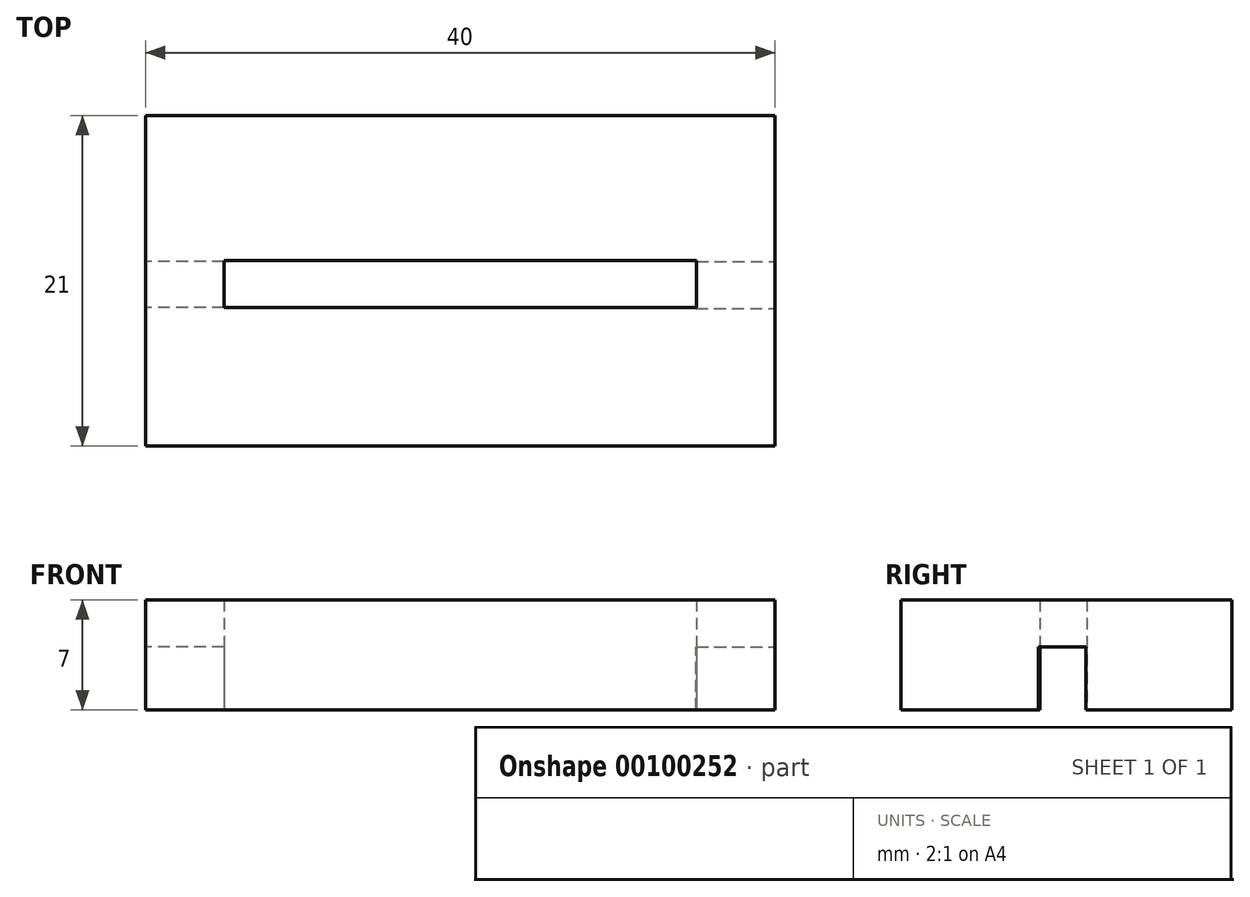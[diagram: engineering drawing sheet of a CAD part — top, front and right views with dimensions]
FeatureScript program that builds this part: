
annotation { "Feature Type Name" : "Feature", "Feature Type Description" : "" }
export const myFeature = defineFeature(function(context is Context, id is Id, definition is map)
    precondition{}
    {
        {
            var Q0;
            Q0=qCreatedBy(makeId("Top.planeOp"),FACE);
            var sketch = newSketch(context, id + "F0", { "sketchPlane" : qUnion([Q0])});
            skLineSegment(sketch, "E0.bottom", {"start": v(0, 0) * mm, "end": v(-40, 0) * mm});
            skLineSegment(sketch, "E0.top", {"start": v(0, -21) * mm, "end": v(-40, -21) * mm});
            skLineSegment(sketch, "E0.left", {"start": v(0, 0) * mm, "end": v(0, -21) * mm});
            skLineSegment(sketch, "E0.right", {"start": v(-40, 0) * mm, "end": v(-40, -21) * mm});
            skLineSegment(sketch, "E1", {"start": v(-20, -9.2) * mm, "end": v(-35, -9.2) * mm});
            skLineSegment(sketch, "E2", {"start": v(-35, -9.2) * mm, "end": v(-5, -9.2) * mm});
            skLineSegment(sketch, "E3", {"start": v(-5, -10.5) * mm, "end": v(-5, -12.2) * mm});
            skLineSegment(sketch, "E4", {"start": v(-5, -12.2) * mm, "end": v(-5, -9.2) * mm});
            skLineSegment(sketch, "E5", {"start": v(-20, -12.2) * mm, "end": v(-35, -12.2) * mm});
            skLineSegment(sketch, "E6", {"start": v(-35, -12.2) * mm, "end": v(-5, -12.2) * mm});
            skLineSegment(sketch, "E7.bottom", {"start": v(-35, -10.5) * mm, "end": v(-35, -10.5) * mm});
            skLineSegment(sketch, "E7.top", {"start": v(-35, -39.85) * mm, "end": v(-35, -39.85) * mm});
            skLineSegment(sketch, "E7.right", {"start": v(-35, -10.5) * mm, "end": v(-35, -12.2) * mm});
            skLineSegment(sketch, "E8.top", {"start": v(-35, 17) * mm, "end": v(-35, 17) * mm});
            skLineSegment(sketch, "E8.left", {"start": v(-35, -12.2) * mm, "end": v(-35, -9.2) * mm});
            skPoint(sketch, "E9.start.orphan", {"position": v(-20, -21) * mm});
            skPoint(sketch, "E10.start.orphan", {"position": v(0, -10.5) * mm});
            skLineSegment(sketch, "E11.right", {"start": v(0, -8.8) * mm, "end": v(0, -12.2) * mm});
            skPoint(sketch, "E12.oppositeSnap0", {"position": v(-40, -10.5) * mm});
            skLineSegment(sketch, "E12.right", {"start": v(-40, -8.8) * mm, "end": v(-40, -12.2) * mm});
            skSolve(sketch);
        }
        {
            var Q0;
            Q0=makeQuery(id+"F0.imprint","IMPRINT",FACE,{"disambiguationData":[TD([[makeQuery(id+"F0.imprint","IMPRINT",EDGE,{"derivedFrom":sQuery(id+"F0.wireOp",EDGE,"E0.bottom")}),1.0]])]});
            extrude(context, id + "F1", {"entities" : qUnion([Q0]), "depth" : 7 * mm});
        }
        {
            var Q0;
            Q0=qCreatedBy(makeId("Top.planeOp"),FACE);
            var sketch = newSketch(context, id + "F2", { "sketchPlane" : qUnion([Q0])});
            skLineSegment(sketch, "E13.bottom", {"start": v(-5.03, -12.27) * mm, "end": v(0, -12.27) * mm});
            skLineSegment(sketch, "E13.top", {"start": v(-5.03, -9.27) * mm, "end": v(0, -9.27) * mm});
            skLineSegment(sketch, "E13.left", {"start": v(-5.03, -12.27) * mm, "end": v(-5.03, -9.27) * mm});
            skLineSegment(sketch, "E13.right", {"start": v(0, -12.27) * mm, "end": v(0, -9.27) * mm});
            skLineSegment(sketch, "E14.bottom", {"start": v(-35, -12.2) * mm, "end": v(-40.25, -12.2) * mm});
            skLineSegment(sketch, "E14.top", {"start": v(-35, -9.26) * mm, "end": v(-40.25, -9.26) * mm});
            skLineSegment(sketch, "E14.left", {"start": v(-35, -12.2) * mm, "end": v(-35, -9.26) * mm});
            skLineSegment(sketch, "E14.right", {"start": v(-40.25, -12.2) * mm, "end": v(-40.25, -9.26) * mm});
            skSolve(sketch);
        }
        {
            var Q0;
            Q0=makeQuery(id+"F2.imprint","IMPRINT",FACE,{"disambiguationData":[TD([[makeQuery(id+"F2.imprint","IMPRINT",EDGE,{"derivedFrom":sQuery(id+"F2.wireOp",EDGE,"E14.bottom")}),-1.0]])]});
            var Q1;
            Q1=makeQuery(id+"F2.imprint","IMPRINT",FACE,{"disambiguationData":[TD([[makeQuery(id+"F2.imprint","IMPRINT",EDGE,{"derivedFrom":sQuery(id+"F2.wireOp",EDGE,"E13.bottom")}),1.0]])]});
            extrude(context, id + "F3", {"entities" : qUnion([Q0, Q1]), "operationType" : NewBodyOperationType.REMOVE, "depth" : 4 * mm});
        }
    });
